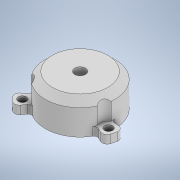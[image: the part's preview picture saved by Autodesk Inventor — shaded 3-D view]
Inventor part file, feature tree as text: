
AUTODESK INVENTOR PART (.ipt)
format: ipt  version: 2022 (Build 260153000, 153)  size: 380,416 bytes
history: native  units: in
note: dims shown in document units (in); Inventor stores cm internally (conversion verified against a paired STEP export)
features: extrude x10, sketch x10, projected_geometry x10, fillet x3, thicken_offset x3, reference x3, other x3, chamfer x1
ambient origin geometry x8: Origin, YZ Plane, XZ Plane, XY Plane, X Axis, Y Axis, Z Axis, Center Point
bodies: Solid1 (feature_tree)
feature tree (43):
  extrude  "Extrusion1"  Depth=1.0in
  extrude  "Extrusion3"  Depth=0.875in
  extrude  "Extrusion4"  Depth=0.0591in
  extrude  "Extrusion5"  Depth=0.05in
  fillet  "Fillet1"  Radius=0.15in
  extrude  "Extrusion6"  Depth=0.15in
  fillet  "Fillet2"  Radius=0.0787in
  chamfer  "Chamfer2"  Distance=7.874in Angle=360.0deg
  extrude  "Extrusion7"  Depth=0.275in
  extrude  "Extrusion8"  Depth=0.125in
  fillet  "Fillet3"  Radius=0.05in
  thicken_offset  "Thicken3"
  thicken_offset  "Thicken4"
  thicken_offset  "Thicken5"
  extrude  "Extrusion9"  TaperAngle=135.0deg  [1 undecoded]
  extrude  "Extrusion10"  Depth=0.125in
  extrude  "Extrusion11"  Depth=0.125in TaperAngle=0.0deg
  sketch  "Sketch1"  dims[d0=0.1575in d1=1.0in]
  sketch  "Sketch3"  dims[d2=0.1181in d3=0.0in d14=0.875in]
  sketch  "Sketch4"  dims[d15=0.3487in d16=0.0in d17=0.0591in]
  projected_geometry  "Projected Loop2"
  projected_geometry  "Projected Loop3"
  sketch  "Sketch5"  dims[d18=0.3in d19=0.05in d20=0.15in]
  projected_geometry  "Projected Loop4"
  sketch  "Sketch8"  dims[d21=0.05in d22=0.15in d23=0.0787in d24=0.0in]
  reference  "Reference5"
  reference  "Reference6"
  reference  "Reference7"
  sketch  "Sketch9"  dims[d28=0.075in]
  projected_geometry  "Projected Loop5"
  projected_geometry  "Projected Loop6"
  sketch  "Sketch10"  dims[d29=45.0deg]
  sketch  "Sketch11"  dims[d30=135.0deg d31=7.874in d33=360.0deg]
  projected_geometry  "Projected Loop7"
  sketch  "Sketch12"  dims[d35=0.0787in d36=0.0in d37=0.275in]
  projected_geometry  "Projected Loop8"
  sketch  "Sketch13"  dims[d38=0.05in d39=0.15in d40=0.05in d41=135.0deg d42=0.05in d43=0.2in d44=0.0in d45=0.05in d46=0.1in d47=0.125in d48=45.0deg d49=0.2362in d50=0.315in d51=0.25in d52=0.0in d53=0.25in d54=0.25in d55=0.25in d56=0.1181in d57=0.0in d58=0.07in d59=0.025in d60=0.025in d61=0.025in d62=0.025in d63=0.025in d64=0.025in d65=1.0in d66=0.0in d67=0.12in d68=0.0in d69=0.25in d70=0.25in d71=0.25in d72=0.12in d73=0.0in]
  projected_geometry  "Projected Loop9"
  projected_geometry  "Projected Loop10"
  projected_geometry  "Projected Loop11"
  parser-record x1  (decoder bookkeeping rows leaked as tree rows — omitted from the tree; the rows remain in map.json)
  other  "Assembly1.iam"
  other  "CubeKnob:1"
note: 1 required parameter value undecoded (feature->parameter linkage not recoverable at this tier; creation-order binding heuristic only, values carry confidence <= 0.55)
note: 1 file-system path scrubbed to <path> (originals preserved in map.json)
